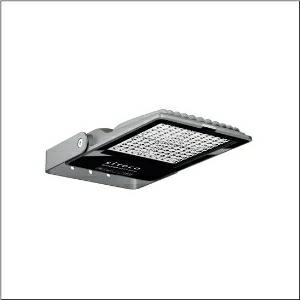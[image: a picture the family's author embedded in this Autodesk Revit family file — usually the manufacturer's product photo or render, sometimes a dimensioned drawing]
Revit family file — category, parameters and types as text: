
# Revit family: sicompact_r__31_mini___pl32_5xa7571f1k23_4385
name_source: partatom
category: Lighting Fixtures
units: mm (PartAtom-declared; Revit-internal decimal feet)

## family parameters
Cut with Voids When Loaded = No
Host = Face
Light Source = No
Part Type = Normal
Room Calculation Point = No
Round Connector Dimension = Use Diameter
Shared = No

## types (1)
- SiCompact® 31 mini  PL32 (1 x LED, 20000 lm, 130 W, 3000K)
    Apparent Load = 130 VA
    CIE Flux Codes = 32 69 98 100 100
    Color Rendering = 70
    Color Temperature = 3000K
    Default Elevation = 1800 mm
    Description = SiCompact® 31 mini, floodlight, primary light control with lens, of plastic, of toughened safety glass, transparent, light distribution: PL32, light emission: direct distribution, primary light characteristic: asymmetric, installation type: surface-mounted, LED, High Power LED, rated luminous flux: 20.000lm, luminous efficacy: 154lm/W, light colour: 730, colour temperature: 3000K, control gear: ECG, with cable, 3x 1.5mm², mains connection: 220..240V, AC, 50/60Hz, connection cable pre-assembled, cable length: 2m, rated input power: 130W, of diecast aluminium, specular, metallic grey (RAL 9006), length: 461mm, width: 261mm, height: 62mm, bracket, of sheet steel, coated, metallic grey (RAL 9006), ON/OFF, protection rating (complete): IP66, insulation class (complete): insulation class I (protective earthing), certification: CE, impact resistance: IK08, permissible operating ambient temperature: -40..+45°C, packaging unit: 1 piece

Light Distribution: PL32
    Height = 62 mm  [stored 0.203412 ft]
    Lamp = 1 x LED
    Lamp Light Flux = 20000 lm
    Lamp Power = 130 W
    Lamp count = 1
    Length = 460 mm
    Luminous efficacy = 154 lm/W
    Manufacturer = Siteco
    ModVariant = No
    Model = 5XA7571F1K23
    Number of Poles = 1
    OnlyDefault = Yes
    Power Factor = 1
    Product Name = SiCompact® 31 mini | PL32
    Product group = floodlight | pylon top
    ProductGroupID = 6101
    Protection Class = Protection class I
    Protection Degree = IP 66
    RLX_Detail_Level = 1
    RlxData = <blob elided: 126697 chars, md5=b3e752c5>
    Socket = socket
    Standby Power = 0 W
    System Light Flux = 20000 lm
    System Power = 130 W
    Type Comments = Product without accessories
    Type Image = l_1006951.jpg
    URL = http://relux.com
    VarID = ---
    Voltage = 0 V
    Weight = 0.00 kg
    Width = 260 mm

note: [stored X ft] marks values corroborated as IEEE doubles in the binary element streams (Revit-internal decimal feet)

## geometry (parser evidence)
native form markers: Blend x4, Sweep x14
no freeform markers — native parametric forms only
